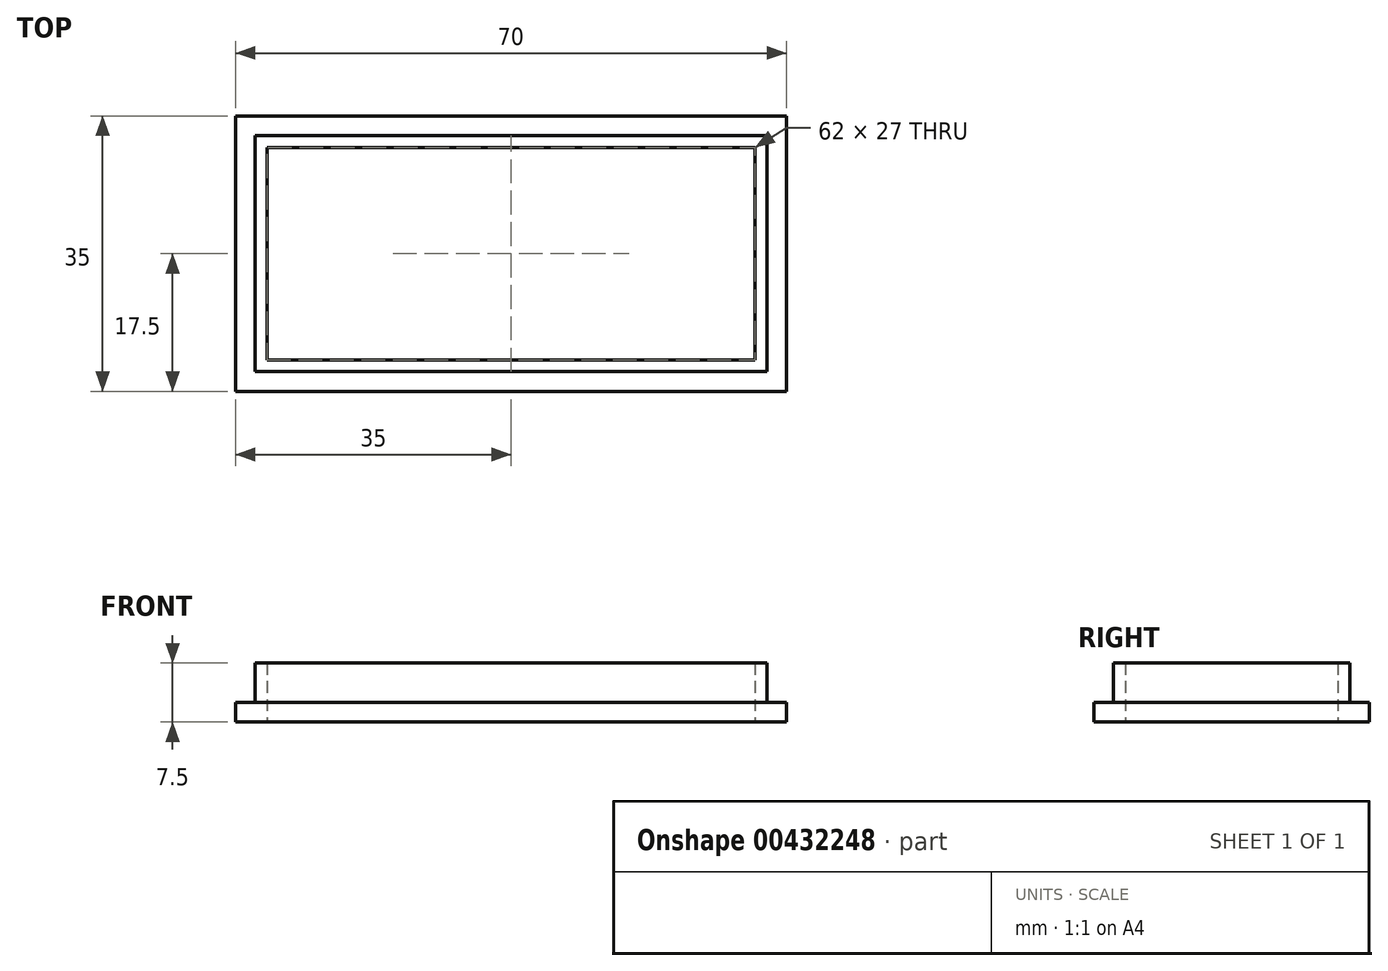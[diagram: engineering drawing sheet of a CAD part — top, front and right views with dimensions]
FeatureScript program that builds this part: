
annotation { "Feature Type Name" : "Feature", "Feature Type Description" : "" }
export const myFeature = defineFeature(function(context is Context, id is Id, definition is map)
    precondition{}
    {
        {
            var Q0;
            Q0=qCreatedBy(makeId("Top.planeOp"),FACE);
            var sketch = newSketch(context, id + "F0", { "sketchPlane" : qUnion([Q0])});
            skLineSegment(sketch, "E0.bottom", {"start": v(35, -17.5) * mm, "end": v(-35, -17.5) * mm});
            skLineSegment(sketch, "E0.top", {"start": v(35, 17.5) * mm, "end": v(-35, 17.5) * mm});
            skLineSegment(sketch, "E0.left", {"start": v(35, -17.5) * mm, "end": v(35, 17.5) * mm});
            skLineSegment(sketch, "E0.right", {"start": v(-35, -17.5) * mm, "end": v(-35, 17.5) * mm});
            skPoint(sketch, "E0.middle", {"position": v(0, 0) * mm});
            skPoint(sketch, "E1.left.end.orphan", {"position": v(32.5, 15) * mm});
            skPoint(sketch, "E2.left.end.orphan", {"position": v(31, 13.5) * mm});
            skPoint(sketch, "E2.bottom.start.orphan", {"position": v(31, -13.5) * mm});
            skPoint(sketch, "E1.bottom.start.orphan", {"position": v(32.5, -15) * mm});
            skPoint(sketch, "E2.right.end.orphan", {"position": v(-31, 13.5) * mm});
            skPoint(sketch, "E2.right.start.orphan", {"position": v(-31, -13.5) * mm});
            skPoint(sketch, "E1.right.end.orphan", {"position": v(-32.5, 15) * mm});
            skPoint(sketch, "E1.right.start.orphan", {"position": v(-32.5, -15) * mm});
            skSolve(sketch);
        }
        {
            var Q0;
            Q0=makeQuery(id+"F0.imprint","IMPRINT",FACE,{"disambiguationData":[TD([[makeQuery(id+"F0.imprint","IMPRINT",EDGE,{"derivedFrom":sQuery(id+"F0.wireOp",EDGE,"E0.bottom")}),-1.0]])]});
            extrude(context, id + "F1", {"entities" : qUnion([Q0]), "depth" : 2.5 * mm});
        }
        {
            var Q0;
            Q0=makeQuery(id+"F1.opExtrude","CAP_FACE",FACE,{"disambiguationData":[OSD([sQuery(id+"F0.wireOp",EDGE,"E0.bottom"),sQuery(id+"F0.wireOp",EDGE,"E0.top"),sQuery(id+"F0.wireOp",EDGE,"E0.left"),sQuery(id+"F0.wireOp",EDGE,"E0.right")])],"isStart":false});
            var sketch = newSketch(context, id + "F2", { "sketchPlane" : qUnion([Q0])});
            skLineSegment(sketch, "E3.bottom", {"start": v(31, -13.5) * mm, "end": v(-31, -13.5) * mm});
            skLineSegment(sketch, "E3.top", {"start": v(31, 13.5) * mm, "end": v(-31, 13.5) * mm});
            skLineSegment(sketch, "E3.left", {"start": v(31, -13.5) * mm, "end": v(31, 13.5) * mm});
            skLineSegment(sketch, "E3.right", {"start": v(-31, -13.5) * mm, "end": v(-31, 13.5) * mm});
            skPoint(sketch, "E3.middle", {"position": v(0, 0) * mm});
            skLineSegment(sketch, "E4.bottom", {"start": v(32.5, -15) * mm, "end": v(-32.5, -15) * mm});
            skLineSegment(sketch, "E4.top", {"start": v(32.5, 15) * mm, "end": v(-32.5, 15) * mm});
            skLineSegment(sketch, "E4.left", {"start": v(32.5, -15) * mm, "end": v(32.5, 15) * mm});
            skLineSegment(sketch, "E4.right", {"start": v(-32.5, -15) * mm, "end": v(-32.5, 15) * mm});
            skSolve(sketch);
        }
        {
            var Q0;
            Q0=makeQuery(id+"F2.imprint","IMPRINT",FACE,{"disambiguationData":[TD([[makeQuery(id+"F2.imprint","IMPRINT",EDGE,{"derivedFrom":sQuery(id+"F2.wireOp",EDGE,"E3.bottom")}),1.0]])]});
            extrude(context, id + "F3", {"entities" : qUnion([Q0]), "operationType" : NewBodyOperationType.ADD, "depth" : 5 * mm});
        }
        {
            var Q0;
            Q0=makeQuery(id+"F3.boolean.opBoolean","SPLIT",FACE,{"disambiguationData":[TD([makeQuery(id+"F3.opExtrude","SWEPT_FACE",FACE,{"disambiguationData":[OSD([sQuery(id+"F2.wireOp",EDGE,"E3.bottom")])]})])],"derivedFrom":makeQuery(id+"F1.opExtrude","CAP_FACE",FACE,{"disambiguationData":[OSD([sQuery(id+"F0.wireOp",EDGE,"E0.bottom"),sQuery(id+"F0.wireOp",EDGE,"E0.top"),sQuery(id+"F0.wireOp",EDGE,"E0.left"),sQuery(id+"F0.wireOp",EDGE,"E0.right")])],"isStart":false})});
            extrude(context, id + "F4", {"entities" : qUnion([Q0]), "operationType" : NewBodyOperationType.REMOVE, "endBound" : BoundingType.UP_TO_NEXT, "oppositeDirection" : true, "depth" : 25 * mm});
        }
        {
            var Q0;
            Q0=makeQuery(id+"F1.opExtrude","CAP_FACE",FACE,{"disambiguationData":[OSD([sQuery(id+"F0.wireOp",EDGE,"E0.bottom"),sQuery(id+"F0.wireOp",EDGE,"E0.top"),sQuery(id+"F0.wireOp",EDGE,"E0.left"),sQuery(id+"F0.wireOp",EDGE,"E0.right")])],"isStart":true});
            var sketch = newSketch(context, id + "F5", { "sketchPlane" : qUnion([Q0])});
            skLineSegment(sketch, "E5.bottom", {"start": v(31, -13.5) * mm, "end": v(-31, -13.5) * mm});
            skLineSegment(sketch, "E5.top", {"start": v(31, 13.5) * mm, "end": v(-31, 13.5) * mm});
            skLineSegment(sketch, "E5.left", {"start": v(31, -13.5) * mm, "end": v(31, 13.5) * mm});
            skLineSegment(sketch, "E5.right", {"start": v(-31, -13.5) * mm, "end": v(-31, 13.5) * mm});
            skPoint(sketch, "E5.middle", {"position": v(0, 0) * mm});
            skSolve(sketch);
        }
        {
            var Q0;
            Q0=qCreatedBy(makeId("Right.planeOp"),FACE);
            cPlane(context, id + "F6", {"entities" : qUnion([Q0]), "cplaneType" : CPlaneType.OFFSET, "offset" : 7 * mm, "width" : 150 * mm, "height" : 150 * mm});
        }
        {
            var Q0;
            Q0=qCreatedBy(makeId("Right.planeOp"),FACE);
            cPlane(context, id + "F7", {"entities" : qUnion([Q0]), "cplaneType" : CPlaneType.OFFSET, "offset" : 14 * mm, "width" : 150 * mm, "height" : 150 * mm});
        }
        {
            var Q0;
            Q0=qCreatedBy(makeId("Right.planeOp"),FACE);
            cPlane(context, id + "F8", {"entities" : qUnion([Q0]), "cplaneType" : CPlaneType.OFFSET, "offset" : 21 * mm, "width" : 150 * mm, "height" : 150 * mm});
        }
        {
            var Q0;
            Q0=qCreatedBy(makeId("Right.planeOp"),FACE);
            cPlane(context, id + "F9", {"entities" : qUnion([Q0]), "cplaneType" : CPlaneType.OFFSET, "offset" : 28 * mm, "width" : 150 * mm, "height" : 150 * mm});
        }
        {
            var Q0;
            Q0=qCreatedBy(makeId("Right.planeOp"),FACE);
            cPlane(context, id + "F10", {"entities" : qUnion([Q0]), "cplaneType" : CPlaneType.OFFSET, "offset" : 35 * mm, "width" : 150 * mm, "height" : 150 * mm});
        }
        {
            var Q0;
            Q0=qCreatedBy(id+"F6.planeOp",FACE);
            var sketch = newSketch(context, id + "F11", { "sketchPlane" : qUnion([Q0])});
            skArc(sketch, "E6", {"start": v(-17.5, 0) * mm, "mid": v(0, -4.99) * mm, "end": v(17.5, 0) * mm});
            skArc(sketch, "E7", {"start": v(-13.5, 0) * mm, "mid": v(0, -3.79) * mm, "end": v(13.5, 0) * mm});
            skSolve(sketch);
        }
        {
            var Q0;
            Q0=qCreatedBy(id+"F7.planeOp",FACE);
            var sketch = newSketch(context, id + "F12", { "sketchPlane" : qUnion([Q0])});
            skArc(sketch, "E8", {"start": v(-17.5, 0) * mm, "mid": v(0, -4.27) * mm, "end": v(17.5, 0) * mm});
            skArc(sketch, "E9", {"start": v(-13.5, 0) * mm, "mid": v(0, -3.07) * mm, "end": v(13.5, 0) * mm});
            skSolve(sketch);
        }
        {
            var Q0;
            Q0=qCreatedBy(id+"F8.planeOp",FACE);
            var sketch = newSketch(context, id + "F13", { "sketchPlane" : qUnion([Q0])});
            skArc(sketch, "E10", {"start": v(-17.5, 0) * mm, "mid": v(0, -2.64) * mm, "end": v(17.5, 0) * mm});
            skArc(sketch, "E11", {"start": v(-13.5, 0) * mm, "mid": v(0, -1.84) * mm, "end": v(13.5, 0) * mm});
            skSolve(sketch);
        }
        {
            var Q0;
            Q0=qCreatedBy(id+"F9.planeOp",FACE);
            var sketch = newSketch(context, id + "F14", { "sketchPlane" : qUnion([Q0])});
            skArc(sketch, "E12", {"start": v(-17.5, 0) * mm, "mid": v(0, -1.33) * mm, "end": v(17.5, 0) * mm});
            skArc(sketch, "E13", {"start": v(-13.5, 0) * mm, "mid": v(0, -0.73) * mm, "end": v(13.5, 0) * mm});
            skSolve(sketch);
        }
        {
            var Q0;
            Q0=qCreatedBy(id+"F10.planeOp",FACE);
            var sketch = newSketch(context, id + "F15", { "sketchPlane" : qUnion([Q0])});
            skLineSegment(sketch, "E14", {"start": v(-17.5, 0) * mm, "end": v(17.5, 0) * mm});
            skSolve(sketch);
        }
        {
            var Q0;
            Q0=qCreatedBy(makeId("Right.planeOp"),FACE);
            var sketch = newSketch(context, id + "F16", { "sketchPlane" : qUnion([Q0])});
            skArc(sketch, "E15", {"start": v(-17.5, 0) * mm, "mid": v(0, -5.33) * mm, "end": v(17.5, 0) * mm});
            skArc(sketch, "E16", {"start": v(-13.5, 0) * mm, "mid": v(0, -4.13) * mm, "end": v(13.5, 0) * mm});
            skSolve(sketch);
        }
        {
            var Q0;
            Q0=sQuery(id+"F16.wireOp",EDGE,"E15");
            var Q1;
            Q1=sQuery(id+"F11.wireOp",EDGE,"E6");
            var Q2;
            Q2=sQuery(id+"F12.wireOp",EDGE,"E8");
            var Q3;
            Q3=sQuery(id+"F13.wireOp",EDGE,"E10");
            var Q4;
            Q4=sQuery(id+"F14.wireOp",EDGE,"E12");
            var Q5;
            Q5=sQuery(id+"F15.wireOp",EDGE,"E14");
            loft(context, id + "F17", {"bodyType" : ToolBodyType.SURFACE, "operationType" : NewBodyOperationType.ADD, "wireProfilesArray" : [{ "wireProfileEntities" : qUnion([Q0]) }, { "wireProfileEntities" : qUnion([Q1]) }, { "wireProfileEntities" : qUnion([Q2]) }, { "wireProfileEntities" : qUnion([Q3]) }, { "wireProfileEntities" : qUnion([Q4]) }, { "wireProfileEntities" : qUnion([Q5]) }]});
        }
        {
            var Q0;
            Q0=sQuery(id+"F16.wireOp",EDGE,"E16");
            var Q1;
            Q1=sQuery(id+"F11.wireOp",EDGE,"E7");
            var Q2;
            Q2=sQuery(id+"F12.wireOp",EDGE,"E9");
            var Q3;
            Q3=sQuery(id+"F13.wireOp",EDGE,"E11");
            var Q4;
            Q4=sQuery(id+"F14.wireOp",EDGE,"E13");
            var Q5;
            Q5=sQuery(id+"F5.wireOp",EDGE,"E5.left");
            loft(context, id + "F18", {"bodyType" : ToolBodyType.SURFACE, "wireProfilesArray" : [{ "wireProfileEntities" : qUnion([Q0]) }, { "wireProfileEntities" : qUnion([Q1]) }, { "wireProfileEntities" : qUnion([Q2]) }, { "wireProfileEntities" : qUnion([Q3]) }, { "wireProfileEntities" : qUnion([Q4]) }, { "wireProfileEntities" : qUnion([Q5]) }]});
        }
    });
